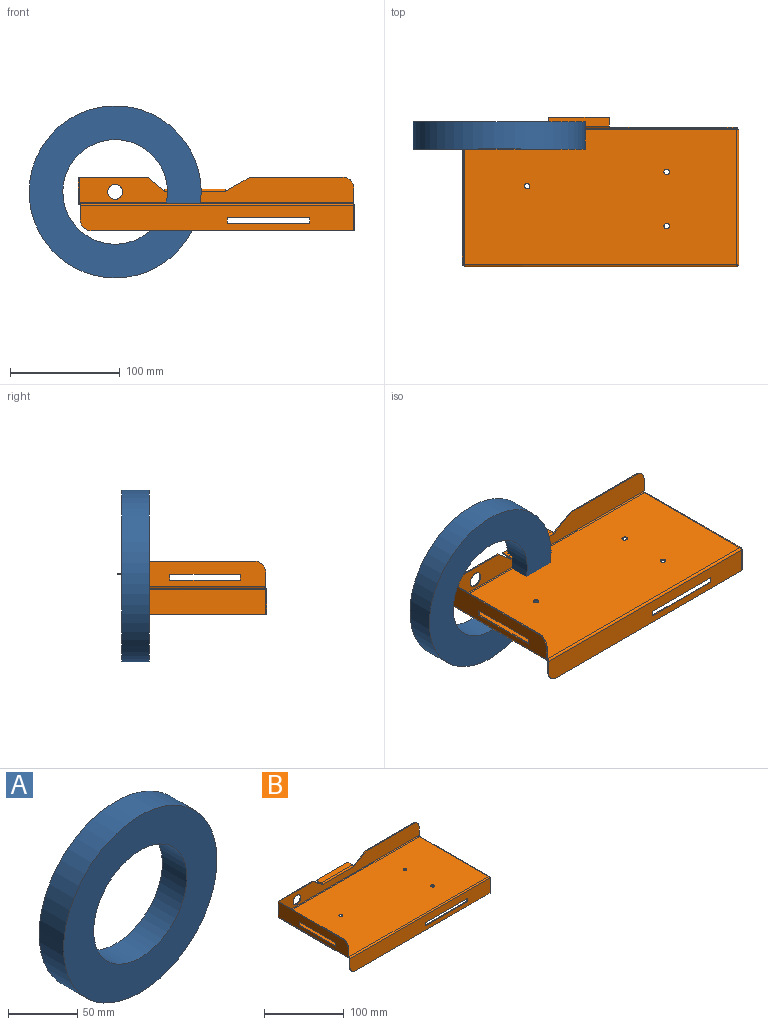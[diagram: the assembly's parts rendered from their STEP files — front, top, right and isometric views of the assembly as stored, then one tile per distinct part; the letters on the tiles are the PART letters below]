
ASSEMBLY  parts=2 mates=1
PART A: 4 faces, bbox 156.7x25x156.7 mm
  f0: cylinder r=47.62mm len=95.24mm, axis (0,1,0), area 7480.2mm2, adj f2,f3
  f1: cylinder r=78.37mm len=156.74mm, axis (0,1,0), area 12310.3mm2, adj f2,f3
  f2: plane 156.74x156.74mm, normal (0,-1,0), area 12171mm2, adj f0,f1
  f3: plane 156.74x156.74mm, normal (0,1,0), area 12171mm2, adj f0,f1
PART B: 70 faces, bbox 252x136x49 mm
  f0: cylinder r=2.5mm len=5mm, axis (0,0,1), area 15.7mm2, adj f3,f4
  f1: cylinder r=2.5mm len=5mm, axis (0,0,1), area 15.7mm2, adj f3,f4
  f2: cylinder r=2.5mm len=5mm, axis (0,0,1), area 15.7mm2, adj f3,f4
  f3: plane 248x123mm, normal (0,0,-1), area 30445.1mm2, adj f0,f1,f2,f5,f6,f29,f44,f59
  f4: plane 248x123mm, normal (0,0,1), area 30445.1mm2, adj f0,f1,f2,f5,f6,f30,f45,f58
  f5: plane 1x0.01mm, normal (0.71,-0.71,0), area 0mm2, adj f3,f4,f57,f66
  f6: plane 1x0.01mm, normal (-0.71,0.71,0), area 0mm2, adj f3,f4,f27,f42
  f7: plane 1x1mm, normal (0,0,-1), area 1mm2, adj f9,f15,f16,f28
  f8: plane 84.31x1mm, normal (0,0,1), area 84.3mm2, adj f14,f15,f16,f17
  f9: plane 13x1mm, normal (1,0,0), area 13mm2, adj f7,f15,f16,f17
  f10: plane 23x1mm, normal (-1,0,0), area 23mm2, adj f11,f15,f16,f27
  f11: plane 62.1x1mm, normal (0,0,1), area 62.1mm2, adj f10,f12,f15,f16
  f12: plane 15.5x12.89mm, normal (0.64,0,0.77), area 20.2mm2, adj f11,f15,f16,f23
  f13: cylinder r=6.79mm len=13.59mm, axis (0,1,0), area 42.7mm2, adj f15,f16
  f14: plane 22.61x12.89mm, normal (-0.5,0,0.87), area 26mm2, adj f8,f15,f16,f24
  f15: plane 249.98x23mm, normal (0,1,0), area 4622.8mm2, adj f7,f8,f9,f10,f11,f12,f13,f14
  f16: plane 249.98x23mm, normal (0,-1,0), area 4622.8mm2, adj f7,f8,f9,f10,f11,f12,f13,f14
  f17: cylinder r=10mm len=10mm, axis (0,1,0), area 15.7mm2, adj f8,f9,f15,f16
  f18: plane 55.46x1mm, normal (0,1,0), area 55.5mm2, adj f19,f20,f21,f22
  f19: plane 8x1mm, normal (1,0,0), area 8mm2, adj f18,f21,f22,f24
  f20: plane 8x1mm, normal (-1,0,0), area 8mm2, adj f18,f21,f22,f23
  f21: plane 55.46x8mm, normal (0,0,-1), area 443.6mm2, adj f18,f19,f20,f26
  f22: plane 55.46x8mm, normal (0,0,1), area 443.6mm2, adj f18,f19,f20,f25
  f23: plane 2x2mm, normal (-1,0,0), area 2.4mm2, adj f12,f20,f25,f26
  f24: plane 2x2mm, normal (1,0,0), area 2.4mm2, adj f14,f19,f25,f26
  f25: cylinder r=2mm len=55.46mm, axis (-1,0,0), area 174.2mm2, adj f16,f22,f23,f24
  f26: cylinder r=1mm len=55.46mm, axis (-1,0,0), area 87.1mm2, adj f15,f21,f23,f24
  f27: bspline ~2x2mm, area 2.6mm2, adj f6,f10,f29,f30
  f28: plane 2x2mm, normal (1,0,0), area 2.4mm2, adj f7,f29,f30,f67
  f29: cylinder r=2mm len=248.98mm, axis (-1,0,0), area 781.1mm2, adj f3,f15,f27,f28
  f30: cylinder r=1mm len=248.98mm, axis (-1,0,0), area 390.5mm2, adj f4,f16,f27,f28
  f31: plane 5.32x1mm, normal (0,1,0), area 5.3mm2, adj f32,f38,f39,f40
  f32: plane 64.28x1mm, normal (0,0,1), area 64.3mm2, adj f31,f33,f39,f40
  f33: plane 5.32x1mm, normal (0,-1,0), area 5.3mm2, adj f32,f38,f39,f40
  f34: plane 114.98x1mm, normal (0,0,1), area 115mm2, adj f35,f39,f40,f41
  f35: plane 23x1mm, normal (0,1,0), area 23mm2, adj f34,f39,f40,f42
  f36: plane 1x1mm, normal (0,0,-1), area 1mm2, adj f37,f39,f40,f43
  f37: plane 13x1mm, normal (0,-1,0), area 13mm2, adj f36,f39,f40,f41
  f38: plane 64.28x1mm, normal (0,0,-1), area 64.3mm2, adj f31,f33,f39,f40
  f39: plane 124.98x23mm, normal (-1,0,0), area 2511.4mm2, adj f31,f32,f33,f34,f35,f36,f37,f38
  f40: plane 124.98x23mm, normal (1,0,0), area 2511.4mm2, adj f31,f32,f33,f34,f35,f36,f37,f38
  f41: cylinder r=10mm len=10mm, axis (-1,0,0), area 15.7mm2, adj f34,f37,f39,f40
  f42: bspline ~2x2mm, area 2.6mm2, adj f6,f35,f44,f45
  f43: plane 2x2mm, normal (0,-1,0), area 2.4mm2, adj f36,f44,f45,f56
  f44: cylinder r=2mm len=123.98mm, axis (0,1,0), area 388.4mm2, adj f3,f39,f42,f43
  f45: cylinder r=1mm len=123.98mm, axis (0,1,0), area 194.2mm2, adj f4,f40,f42,f43
  f46: plane 75x1mm, normal (0,0,1), area 75mm2, adj f47,f52,f53,f54
  f47: plane 5x1mm, normal (-1,0,0), area 5mm2, adj f46,f48,f53,f54
  f48: plane 75x1mm, normal (0,0,-1), area 75mm2, adj f47,f52,f53,f54
  f49: plane 238.98x1mm, normal (0,0,-1), area 239mm2, adj f51,f53,f54,f55
  f50: plane 13x1mm, normal (-1,0,0), area 13mm2, adj f53,f54,f55,f56
  f51: plane 23x1mm, normal (1,0,0), area 23mm2, adj f49,f53,f54,f57
  f52: plane 5x1mm, normal (1,0,0), area 5mm2, adj f46,f48,f53,f54
  f53: plane 248.98x23mm, normal (0,1,0), area 5330.1mm2, adj f46,f47,f48,f49,f50,f51,f52,f55
  f54: plane 248.98x23mm, normal (0,-1,0), area 5330.1mm2, adj f46,f47,f48,f49,f50,f51,f52,f55
  f55: cylinder r=10mm len=10mm, axis (0,1,0), area 15.7mm2, adj f49,f50,f53,f54
  f56: plane 2x2mm, normal (-1,0,0), area 2.4mm2, adj f43,f50,f58,f59
  f57: bspline ~2x2mm, area 2.6mm2, adj f5,f51,f58,f59
  f58: cylinder r=2mm len=248.98mm, axis (-1,0,0), area 781.1mm2, adj f4,f54,f56,f57
  f59: cylinder r=1mm len=248.98mm, axis (-1,0,0), area 390.5mm2, adj f3,f53,f56,f57
  f60: plane 113.98x1mm, normal (0,0,-1), area 114mm2, adj f61,f63,f64,f65
  f61: plane 23x1mm, normal (0,-1,0), area 23mm2, adj f60,f63,f64,f66
  f62: plane 13x1mm, normal (0,1,0), area 13mm2, adj f63,f64,f65,f67
  f63: plane 123.98x23mm, normal (-1,0,0), area 2830.1mm2, adj f60,f61,f62,f65,f69
  f64: plane 123.98x23mm, normal (1,0,0), area 2830.1mm2, adj f60,f61,f62,f65,f68
  f65: cylinder r=10mm len=10mm, axis (-1,0,0), area 15.7mm2, adj f60,f62,f63,f64
  f66: bspline ~2x2mm, area 2.6mm2, adj f5,f61,f68,f69
  f67: plane 2x2mm, normal (0,1,0), area 2.4mm2, adj f28,f62,f68,f69
  f68: cylinder r=2mm len=123.98mm, axis (0,-1,0), area 388.4mm2, adj f4,f64,f66,f67
  f69: cylinder r=1mm len=123.98mm, axis (0,-1,0), area 194.2mm2, adj f3,f63,f66,f67
PLACE A t=(-87.36,71.02,18.35)mm
PLACE B t=(4.93,2.52,6.81)mm
MATE revolute A.f1 <-> B.f13  axis (0,1,0) through (-87.36,71.02,18.35)mm
